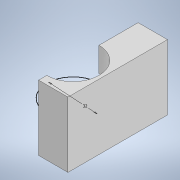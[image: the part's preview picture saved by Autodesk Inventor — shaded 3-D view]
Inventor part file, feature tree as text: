
AUTODESK INVENTOR PART (.ipt)
format: ipt  version: 2022 (Build 260153000, 153)  size: 110,080 bytes
history: native  units: mm
features: sketch x3, extrude x3, split x1, boolean_combine x1
ambient origin geometry x8: Origin, YZ Plane, XZ Plane, XY Plane, X Axis, Y Axis, Z Axis, Center Point
bodies: Solid1 (feature_tree), Solid2 (feature_tree)
feature tree (8):
  sketch  "Sketch1"  dims[d0=32.0mm d1=40.0mm d2=0.0mm]
  extrude  "Extrusion1"  Depth=40.0mm TaperAngle=0.0deg
  extrude  "Extrusion2"  Depth=10.0mm TaperAngle=0.0deg
  split  "Split1"
  extrude  "Extrusion3"  Depth=40.0mm
  boolean_combine  "Combine1"
  sketch  "Sketch2"  dims[d3=10.0mm d4=40.0mm d5=0.0mm]
  sketch  "Sketch3"  dims[d8=18.0mm d9=0.0mm d10=40.0mm d11=61.0mm]
